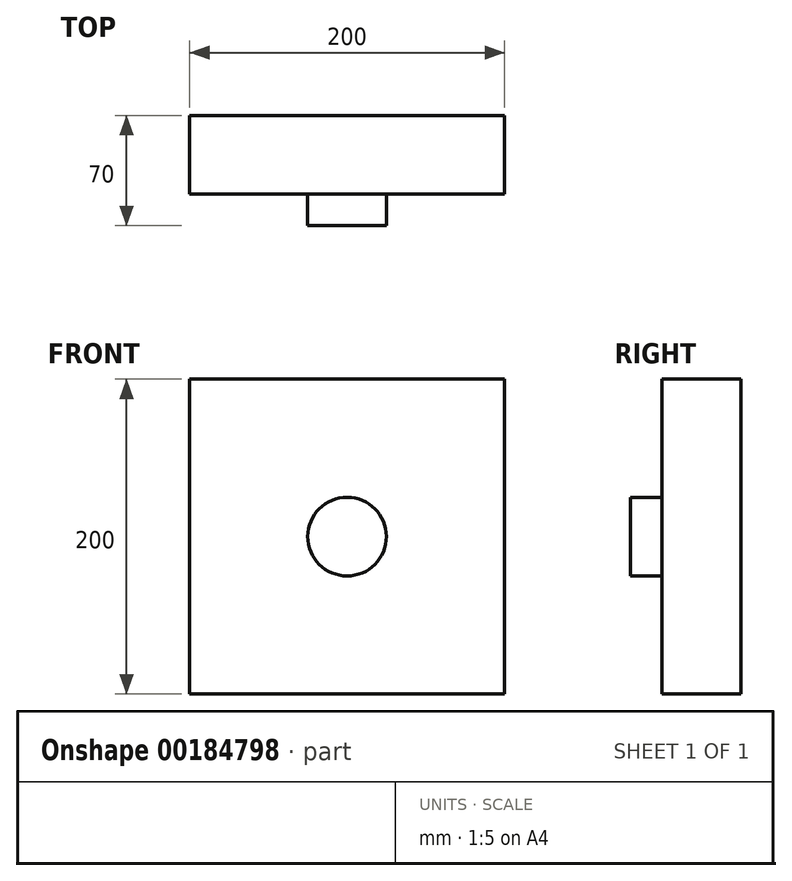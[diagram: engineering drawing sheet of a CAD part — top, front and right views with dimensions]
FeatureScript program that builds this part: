
annotation { "Feature Type Name" : "Feature", "Feature Type Description" : "" }
export const myFeature = defineFeature(function(context is Context, id is Id, definition is map)
    precondition{}
    {
        {
            var Q0;
            Q0=qCreatedBy(makeId("Front.planeOp"),FACE);
            var sketch = newSketch(context, id + "F0", { "sketchPlane" : qUnion([Q0])});
            skLineSegment(sketch, "E0", {"start": v(0, 0) * mm, "end": v(200, 0) * mm});
            skLineSegment(sketch, "E1", {"start": v(200, 0) * mm, "end": v(200, 200) * mm});
            skLineSegment(sketch, "E2", {"start": v(200, 200) * mm, "end": v(0, 200) * mm});
            skLineSegment(sketch, "E3", {"start": v(0, 200) * mm, "end": v(0, 0) * mm});
            skSolve(sketch);
        }
        {
            var Q0;
            Q0=makeQuery(id+"F0.imprint","IMPRINT",FACE,{"disambiguationData":[TD([[makeQuery(id+"F0.imprint","IMPRINT",EDGE,{"derivedFrom":sQuery(id+"F0.wireOp",EDGE,"E0")}),1.0]])]});
            extrude(context, id + "F1", {"entities" : qUnion([Q0]), "depth" : 50 * mm});
        }
        {
            var Q0;
            Q0=makeQuery(id+"F1.opExtrude","CAP_FACE",FACE,{"disambiguationData":[OSD([sQuery(id+"F0.wireOp",EDGE,"E0"),sQuery(id+"F0.wireOp",EDGE,"E1"),sQuery(id+"F0.wireOp",EDGE,"E2"),sQuery(id+"F0.wireOp",EDGE,"E3")])],"isStart":false});
            var sketch = newSketch(context, id + "F2", { "sketchPlane" : qUnion([Q0])});
            skLineSegment(sketch, "E4", {"start": v(0, 0) * mm, "end": v(200, 200) * mm, "construction": true});
            skLineSegment(sketch, "E5", {"start": v(0, 200) * mm, "end": v(200, 0) * mm, "construction": true});
            skCircle(sketch, "E6", {"center": v(100, 100) * mm, "radius": 25 * mm});
            skSolve(sketch);
        }
        {
            var Q0;
            Q0 = qSketchRegion(id + "F2", true);
            extrude(context, id + "F3", {"entities" : qUnion([Q0]), "operationType" : NewBodyOperationType.ADD, "depth" : 20 * mm});
        }
    });
